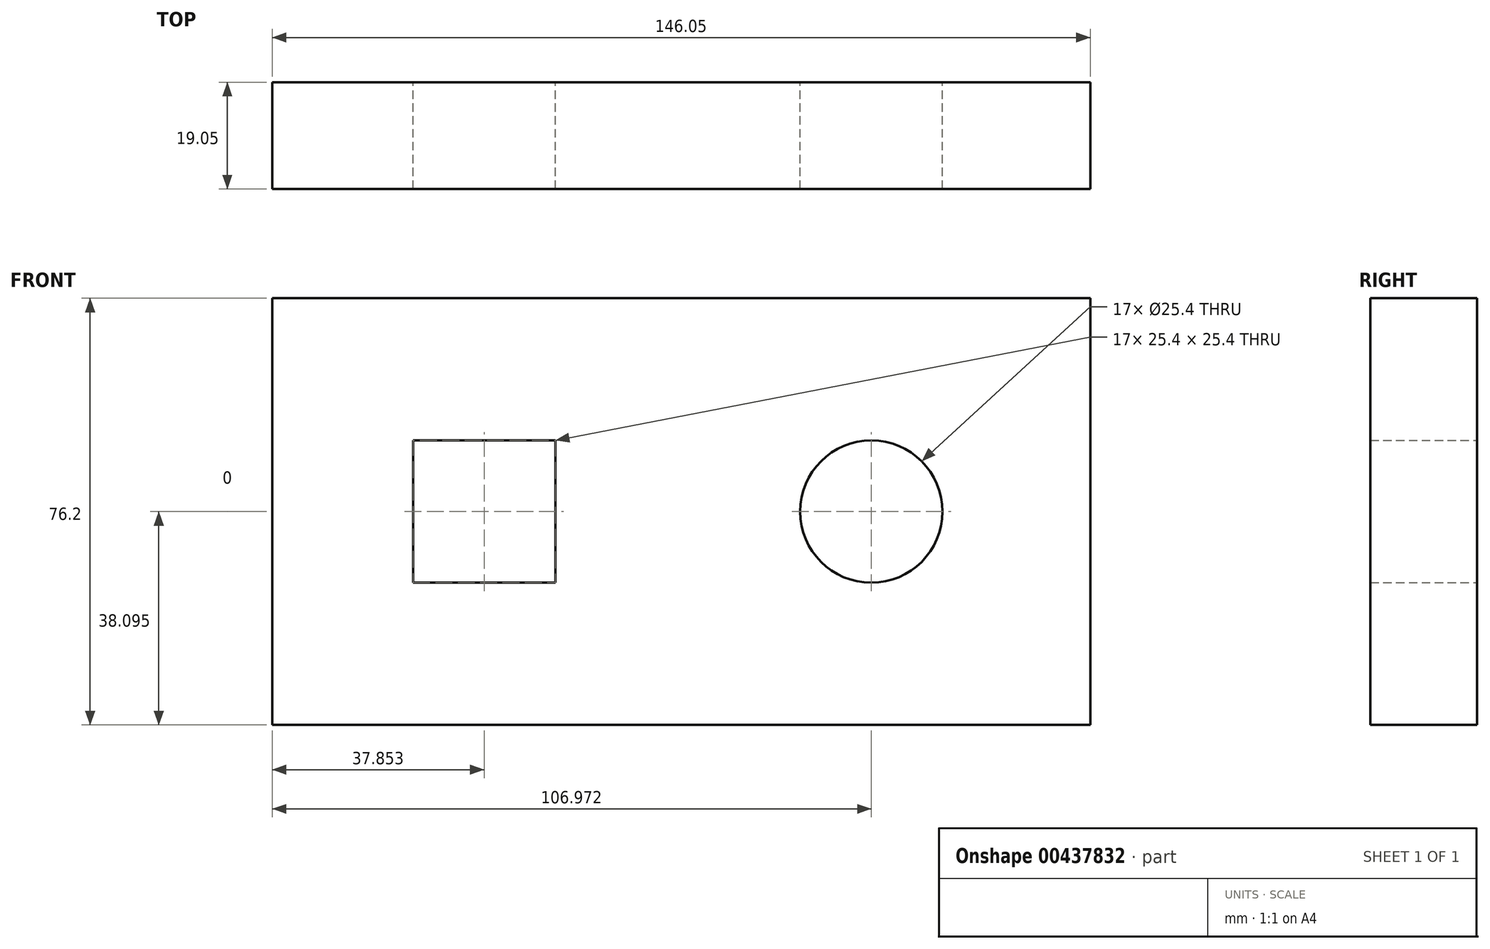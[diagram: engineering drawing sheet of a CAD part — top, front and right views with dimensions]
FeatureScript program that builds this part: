
annotation { "Feature Type Name" : "Feature", "Feature Type Description" : "" }
export const myFeature = defineFeature(function(context is Context, id is Id, definition is map)
    precondition{}
    {
        {
            var Q0;
            Q0=qCreatedBy(makeId("Front.planeOp"),FACE);
            var sketch = newSketch(context, id + "F0", { "sketchPlane" : qUnion([Q0])});
            skLineSegment(sketch, "E0.bottom", {"start": v(-97.75, 50.72) * mm, "end": v(48.3, 50.72) * mm});
            skLineSegment(sketch, "E0.top", {"start": v(-97.75, -25.48) * mm, "end": v(48.3, -25.48) * mm});
            skLineSegment(sketch, "E0.left", {"start": v(-97.75, 50.72) * mm, "end": v(-97.75, -25.48) * mm});
            skLineSegment(sketch, "E0.right", {"start": v(48.3, 50.72) * mm, "end": v(48.3, -25.48) * mm});
            skCircle(sketch, "E1", {"center": v(9.22, 12.62) * mm, "radius": 12.7 * mm});
            skLineSegment(sketch, "E2", {"start": v(-72.6, 12.62) * mm, "end": v(-72.6, 25.32) * mm});
            skLineSegment(sketch, "E3", {"start": v(-72.6, 12.62) * mm, "end": v(-72.6, -0.08) * mm});
            skLineSegment(sketch, "E4", {"start": v(-72.6, -0.08) * mm, "end": v(-47.2, -0.08) * mm});
            skLineSegment(sketch, "E5", {"start": v(-47.2, -0.08) * mm, "end": v(-47.2, 25.32) * mm});
            skLineSegment(sketch, "E6", {"start": v(-47.2, 25.32) * mm, "end": v(-72.6, 25.32) * mm});
            skPoint(sketch, "E7.orphan", {"position": v(-24.72, 50.72) * mm});
            skPoint(sketch, "E8.end.orphan", {"position": v(-24.72, -25.48) * mm});
            skPoint(sketch, "E9.trimOffspring.end.orphan", {"position": v(-97.75, 12.62) * mm});
            skPoint(sketch, "E10.start.orphan", {"position": v(48.3, 12.62) * mm});
            skSolve(sketch);
        }
        {
            var Q0;
            Q0 = qSketchRegion(id + "F0", true);
            extrude(context, id + "F1", {"entities" : qUnion([Q0]), "depth" : 19.05 * mm});
        }
    });
